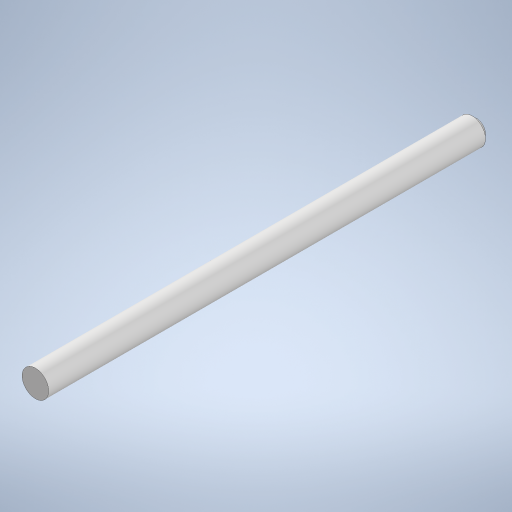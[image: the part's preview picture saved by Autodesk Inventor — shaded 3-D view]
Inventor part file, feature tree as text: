
AUTODESK INVENTOR PART (.ipt)
format: ipt  version: 2024.1 (Build 281209000, 209)  size: 239,616 bytes
history: native  units: in
note: dims shown in document units (in); Inventor stores cm internally (conversion verified against a paired STEP export)
features: extrude x1, chamfer x1, sketch x1
ambient origin geometry x8: Origin, YZ Plane, XZ Plane, XY Plane, X Axis, Y Axis, Z Axis, Center Point
bodies: Solid1 (feature_tree)
feature tree (3):
  extrude  "Extrusion1"  Depth=1.9685in TaperAngle=0.0deg
  chamfer  "Chamfer1"  Distance=0.0197in Angle=45.0deg
  sketch  "Sketch1"  dims[d0=0.1181in d1=1.9685in d2=0.0in d3=0.0197in d4=0.125in d5=45.0deg]
